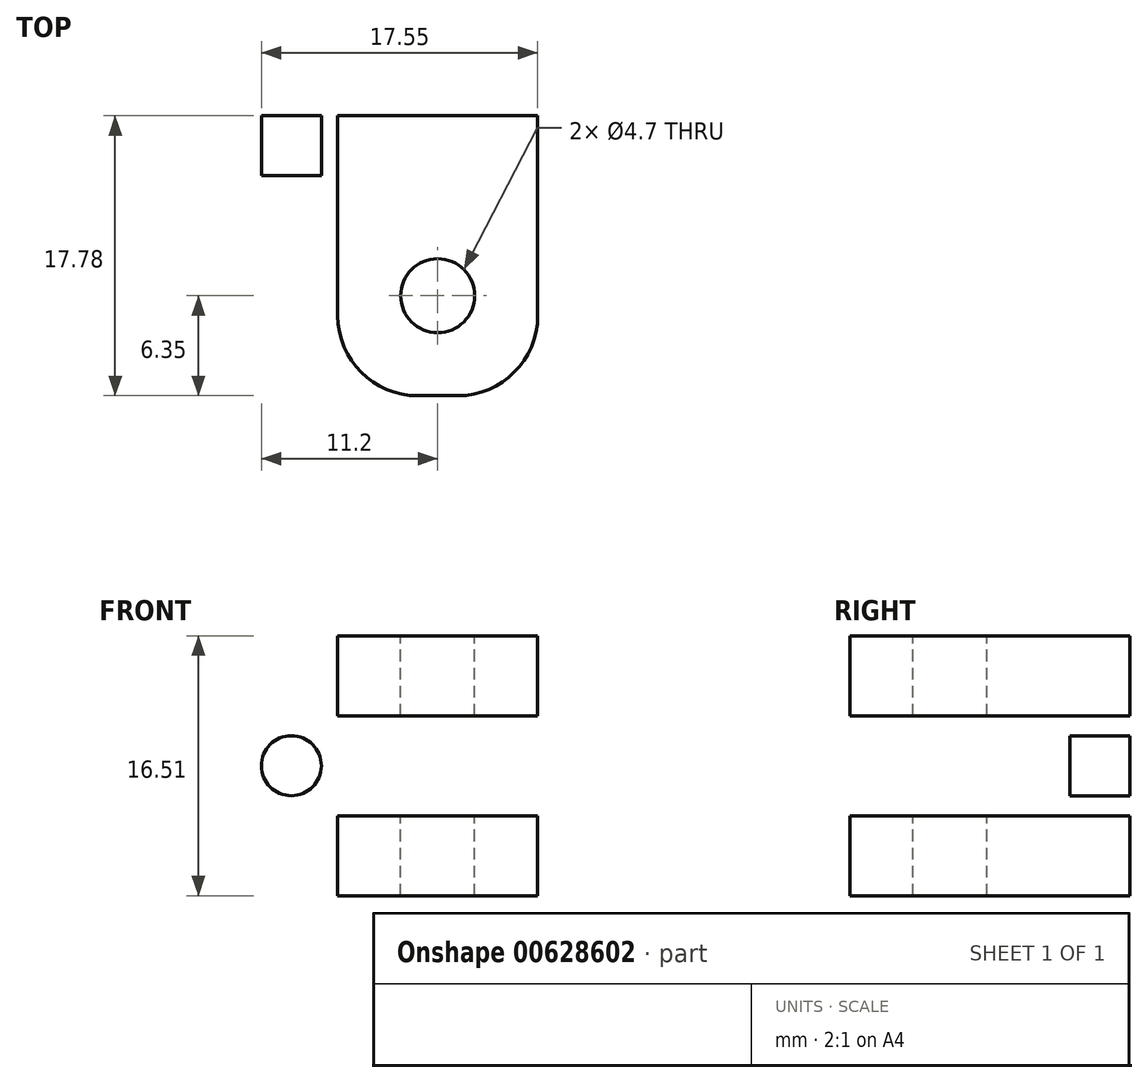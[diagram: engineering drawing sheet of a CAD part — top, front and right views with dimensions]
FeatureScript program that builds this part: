
annotation { "Feature Type Name" : "Feature", "Feature Type Description" : "" }
export const myFeature = defineFeature(function(context is Context, id is Id, definition is map)
    precondition{}
    {
        {
            var Q0;
            Q0=qCreatedBy(makeId("Right.planeOp"),FACE);
            var sketch = newSketch(context, id + "F0", { "sketchPlane" : qUnion([Q0])});
            skLineSegment(sketch, "E0", {"start": v(0, 0) * mm, "end": v(0, -16.51) * mm});
            skLineSegment(sketch, "E1", {"start": v(0, 0) * mm, "end": v(-3.81, 0) * mm});
            skLineSegment(sketch, "E2", {"start": v(-3.81, 0) * mm, "end": v(-3.81, -16.51) * mm});
            skLineSegment(sketch, "E3", {"start": v(-3.81, -16.51) * mm, "end": v(0, -16.51) * mm});
            skSolve(sketch);
        }
        {
            var Q0;
            Q0=makeQuery(id+"F0.imprint","IMPRINT",FACE,{"disambiguationData":[TD([[makeQuery(id+"F0.imprint","IMPRINT",EDGE,{"derivedFrom":sQuery(id+"F0.wireOp",EDGE,"E0")}),-1.0]])]});
            extrude(context, id + "F1", {"entities" : qUnion([Q0]), "depth" : 25.4 * mm, "offsetDistance" : 25.4 * mm});
        }
        {
            var Q0;
            Q0=makeQuery(id+"F1.opExtrude","SWEPT_FACE",FACE,{"disambiguationData":[OSD([sQuery(id+"F0.wireOp",EDGE,"E2")])]});
            var sketch = newSketch(context, id + "F2", { "sketchPlane" : qUnion([Q0])});
            skLineSegment(sketch, "E4", {"start": v(12.7, 0) * mm, "end": v(19.05, 0) * mm});
            skLineSegment(sketch, "E5", {"start": v(12.7, 0) * mm, "end": v(6.35, 0) * mm});
            skLineSegment(sketch, "E6", {"start": v(6.35, 0) * mm, "end": v(6.35, -5.08) * mm});
            skLineSegment(sketch, "E7", {"start": v(6.35, -5.08) * mm, "end": v(19.05, -5.08) * mm});
            skLineSegment(sketch, "E8", {"start": v(19.05, -5.08) * mm, "end": v(19.05, 0) * mm});
            skLineSegment(sketch, "E9", {"start": v(19.05, -16.51) * mm, "end": v(19.05, -11.43) * mm});
            skLineSegment(sketch, "E10", {"start": v(19.05, -11.43) * mm, "end": v(6.35, -11.43) * mm});
            skLineSegment(sketch, "E11", {"start": v(6.35, -11.43) * mm, "end": v(6.35, -16.51) * mm});
            skLineSegment(sketch, "E12", {"start": v(19.05, -16.51) * mm, "end": v(6.35, -16.51) * mm});
            skSolve(sketch);
        }
        {
            var Q0;
            Q0=makeQuery(id+"F2.imprint","IMPRINT",FACE,{"disambiguationData":[TD([[makeQuery(id+"F2.imprint","IMPRINT",EDGE,{"derivedFrom":sQuery(id+"F2.wireOp",EDGE,"E4")}),1.0]])]});
            var Q1;
            Q1=makeQuery(id+"F2.imprint","IMPRINT",FACE,{"disambiguationData":[TD([[makeQuery(id+"F2.imprint","IMPRINT",EDGE,{"derivedFrom":sQuery(id+"F2.wireOp",EDGE,"E9")}),1.0]])]});
            extrude(context, id + "F3", {"entities" : qUnion([Q0, Q1]), "operationType" : NewBodyOperationType.ADD, "depth" : 13.97 * mm, "offsetDistance" : 25.4 * mm});
        }
        {
            var Q0;
            Q0=makeQuery(id+"F3.opExtrude","CAP_EDGE",EDGE,{"disambiguationData":[OSD([sQuery(id+"F2.wireOp",EDGE,"E8")])],"isStart":false});
            var Q1;
            Q1=makeQuery(id+"F3.opExtrude","CAP_EDGE",EDGE,{"disambiguationData":[OSD([sQuery(id+"F2.wireOp",EDGE,"E6")])],"isStart":false});
            var Q2;
            Q2=makeQuery(id+"F3.opExtrude","CAP_EDGE",EDGE,{"disambiguationData":[OSD([sQuery(id+"F2.wireOp",EDGE,"E9")])],"isStart":false});
            var Q3;
            Q3=makeQuery(id+"F3.opExtrude","CAP_EDGE",EDGE,{"disambiguationData":[OSD([sQuery(id+"F2.wireOp",EDGE,"E11")])],"isStart":false});
            fillet(context, id + "F4", {"entities" : qUnion([Q0, Q1, Q2, Q3]), "radius" : 5.08 * mm, "tangentPropagation" : true, "allowEdgeOverflow" : false});
        }
        {
            var Q0;
            Q0=makeQuery(id+"F3.boolean.opBoolean","MERGE",FACE,{"derivedFrom":[makeQuery(id+"F1.opExtrude","SWEPT_FACE",FACE,{"disambiguationData":[OSD([sQuery(id+"F0.wireOp",EDGE,"E1")])]}),makeQuery(id+"F3.opExtrude","SWEPT_FACE",FACE,{"disambiguationData":[OSD([sQuery(id+"F2.wireOp",EDGE,"E4"),sQuery(id+"F2.wireOp",EDGE,"E5")])]})]});
            var sketch = newSketch(context, id + "F5", { "sketchPlane" : qUnion([Q0])});
            skLineSegment(sketch, "E13", {"start": v(12.7, -17.78) * mm, "end": v(12.7, -11.43) * mm});
            skCircle(sketch, "E14", {"center": v(12.7, -11.43) * mm, "radius": 2.35 * mm});
            skSolve(sketch);
        }
        {
            var Q0;
            Q0=makeQuery(id+"F5.imprint","IMPRINT",FACE,{"disambiguationData":[TD([[makeQuery(id+"F5.imprint","IMPRINT",EDGE,{"derivedFrom":sQuery(id+"F5.wireOp",EDGE,"E14")}),1.0]])]});
            extrude(context, id + "F6", {"entities" : qUnion([Q0]), "operationType" : NewBodyOperationType.REMOVE, "oppositeDirection" : true, "depth" : 25.4 * mm, "offsetDistance" : 25.4 * mm});
        }
        {
            var Q0;
            Q0=makeQuery(id+"F1.opExtrude","SWEPT_FACE",FACE,{"disambiguationData":[OSD([sQuery(id+"F0.wireOp",EDGE,"E2")])]});
            var sketch = newSketch(context, id + "F7", { "sketchPlane" : qUnion([Q0])});
            skLineSegment(sketch, "E15", {"start": v(12.68, 0) * mm, "end": v(25.4, 0) * mm});
            skLineSegment(sketch, "E16", {"start": v(12.68, 0.1) * mm, "end": v(12.68, 0) * mm});
            skPoint(sketch, "E16.endSnap0", {"position": v(25.4, -8.26) * mm});
            skCircle(sketch, "E17", {"center": v(21.95, -8.26) * mm, "radius": 1.9 * mm});
            skCircle(sketch, "E18.MirrorC", {"center": v(3.4, -8.26) * mm, "radius": 1.9 * mm});
            skPoint(sketch, "E19.orphan", {"position": v(12.68, -8.26) * mm});
            skPoint(sketch, "E20.orphan", {"position": v(0, 0) * mm});
            skPoint(sketch, "E21.end.orphan", {"position": v(12.7, 0) * mm});
            skSolve(sketch);
        }
        {
            var Q0;
            Q0=makeQuery(id+"F7.imprint","IMPRINT",FACE,{"disambiguationData":[TD([[makeQuery(id+"F7.imprint","IMPRINT",EDGE,{"derivedFrom":sQuery(id+"F7.wireOp",EDGE,"E18.MirrorC")}),-1.0]])]});
            var Q1;
            Q1=makeQuery(id+"F7.imprint","IMPRINT",FACE,{"disambiguationData":[TD([[makeQuery(id+"F7.imprint","IMPRINT",EDGE,{"derivedFrom":sQuery(id+"F7.wireOp",EDGE,"E17")}),1.0]])]});
            extrude(context, id + "F8", {"entities" : qUnion([Q0, Q1]), "operationType" : NewBodyOperationType.REMOVE, "oppositeDirection" : true, "depth" : 25.4 * mm, "offsetDistance" : 25.4 * mm});
        }
    });
